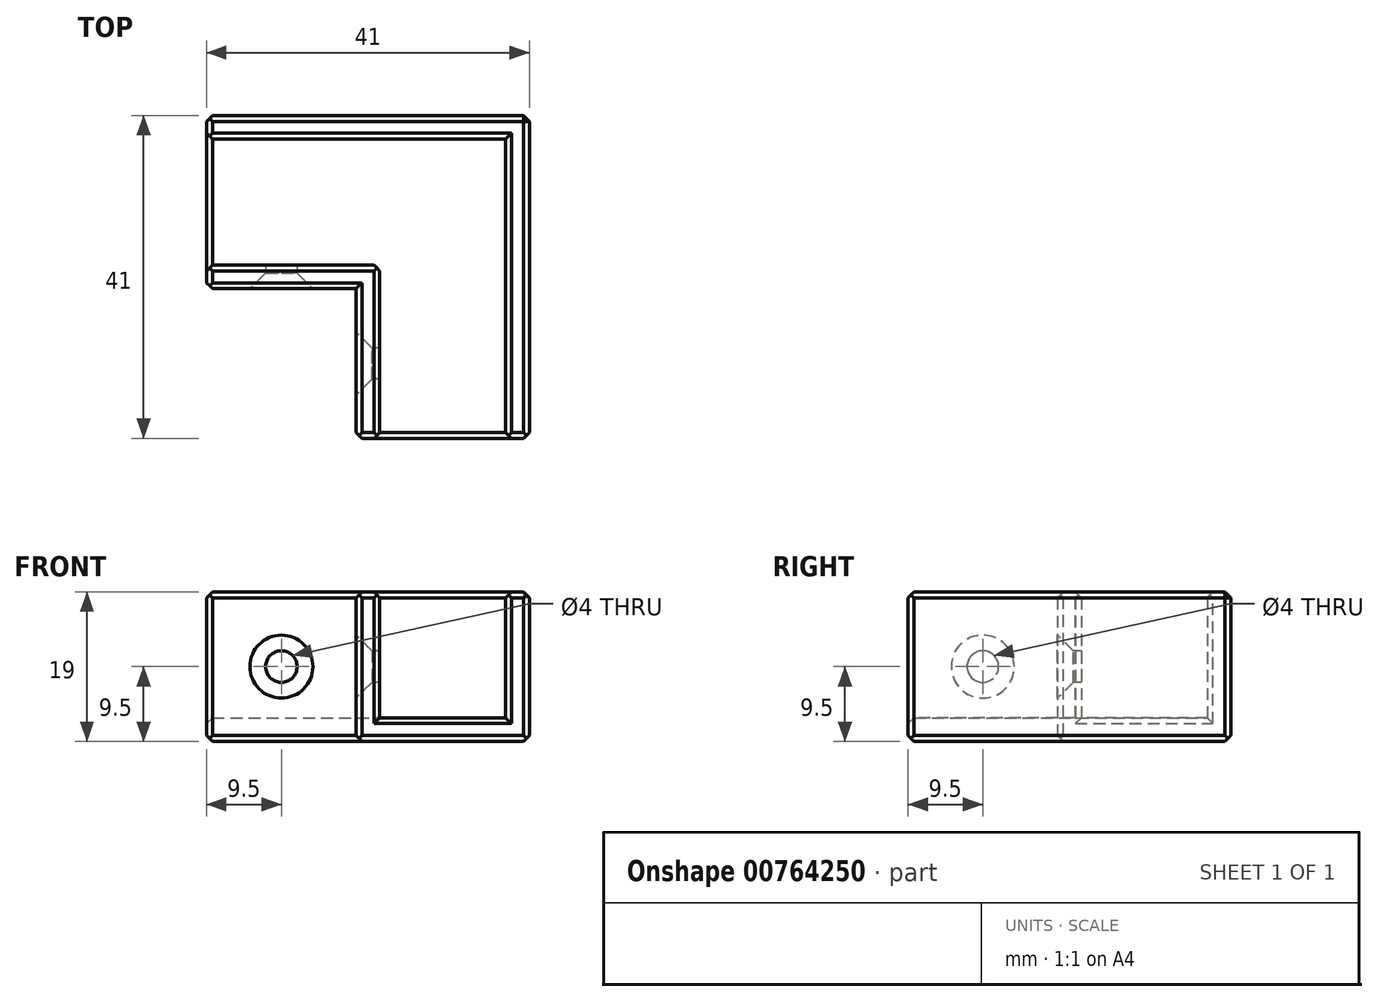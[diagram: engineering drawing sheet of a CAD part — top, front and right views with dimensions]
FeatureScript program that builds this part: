
annotation { "Feature Type Name" : "Feature", "Feature Type Description" : "" }
export const myFeature = defineFeature(function(context is Context, id is Id, definition is map)
    precondition{}
    {
        {
            var Q0;
            Q0=qCreatedBy(makeId("Top.planeOp"),FACE);
            var sketch = newSketch(context, id + "F0", { "sketchPlane" : qUnion([Q0])});
            skLineSegment(sketch, "E0.bottom", {"start": v(0, 0) * mm, "end": v(41, 0) * mm});
            skLineSegment(sketch, "E0.top", {"start": v(0, 22) * mm, "end": v(41, 22) * mm});
            skLineSegment(sketch, "E0.left", {"start": v(0, 0) * mm, "end": v(0, 22) * mm});
            skLineSegment(sketch, "E0.right", {"start": v(41, 0) * mm, "end": v(41, 22) * mm});
            skLineSegment(sketch, "E1", {"start": v(0, 0) * mm, "end": v(19, 0) * mm});
            skLineSegment(sketch, "E2.bottom", {"start": v(19, 0) * mm, "end": v(41, 0) * mm});
            skLineSegment(sketch, "E2.top", {"start": v(19, -19) * mm, "end": v(41, -19) * mm});
            skLineSegment(sketch, "E2.left", {"start": v(19, 0) * mm, "end": v(19, -19) * mm});
            skLineSegment(sketch, "E2.right", {"start": v(41, 0) * mm, "end": v(41, -19) * mm});
            skSolve(sketch);
        }
        {
            var Q0;
            Q0=makeQuery(id+"F0.imprint","IMPRINT",FACE,{"disambiguationData":[TD([[makeQuery(id+"F0.imprint","IMPRINT",EDGE,{"derivedFrom":sQuery(id+"F0.wireOp",EDGE,"E0.top")}),-1.0]])]});
            var Q1;
            Q1=makeQuery(id+"F0.imprint","IMPRINT",FACE,{"disambiguationData":[TD([[makeQuery(id+"F0.imprint","IMPRINT",EDGE,{"derivedFrom":sQuery(id+"F0.wireOp",EDGE,"E2.top")}),1.0]])]});
            extrude(context, id + "F1", {"entities" : qUnion([Q0, Q1]), "depth" : 3 * mm, "offsetDistance" : 25 * mm});
        }
        {
            var Q0;
            Q0=makeQuery(id+"F1.opExtrude","CAP_FACE",FACE,{"disambiguationData":[OSD([sQuery(id+"F0.wireOp",EDGE,"E0.bottom"),sQuery(id+"F0.wireOp",EDGE,"E0.top"),sQuery(id+"F0.wireOp",EDGE,"E0.left"),sQuery(id+"F0.wireOp",EDGE,"E0.right"),sQuery(id+"F0.wireOp",EDGE,"E2.top"),sQuery(id+"F0.wireOp",EDGE,"E2.left"),sQuery(id+"F0.wireOp",EDGE,"E2.right")])],"isStart":false});
            var sketch = newSketch(context, id + "F2", { "sketchPlane" : qUnion([Q0])});
            skLineSegment(sketch, "E3.bottom", {"start": v(0, 22) * mm, "end": v(41, 22) * mm});
            skLineSegment(sketch, "E3.top", {"start": v(0, 19) * mm, "end": v(41, 19) * mm});
            skLineSegment(sketch, "E3.left", {"start": v(0, 22) * mm, "end": v(0, 19) * mm});
            skLineSegment(sketch, "E3.right", {"start": v(41, 22) * mm, "end": v(41, 19) * mm});
            skLineSegment(sketch, "E4.bottom", {"start": v(19, 0) * mm, "end": v(0, 0) * mm});
            skLineSegment(sketch, "E4.top", {"start": v(19, 3) * mm, "end": v(0, 3) * mm});
            skLineSegment(sketch, "E4.left", {"start": v(19, 0) * mm, "end": v(19, 3) * mm});
            skLineSegment(sketch, "E4.right", {"start": v(0, 0) * mm, "end": v(0, 3) * mm});
            skLineSegment(sketch, "E5.bottom", {"start": v(19, 3) * mm, "end": v(22, 3) * mm});
            skLineSegment(sketch, "E5.top", {"start": v(19, -19) * mm, "end": v(22, -19) * mm});
            skLineSegment(sketch, "E5.left", {"start": v(19, 3) * mm, "end": v(19, -19) * mm});
            skLineSegment(sketch, "E5.right", {"start": v(22, 3) * mm, "end": v(22, -19) * mm});
            skLineSegment(sketch, "E6.bottom", {"start": v(41, -19) * mm, "end": v(38, -19) * mm});
            skLineSegment(sketch, "E6.top", {"start": v(41, 19) * mm, "end": v(38, 19) * mm});
            skLineSegment(sketch, "E6.left", {"start": v(41, -19) * mm, "end": v(41, 19) * mm});
            skLineSegment(sketch, "E6.right", {"start": v(38, -19) * mm, "end": v(38, 19) * mm});
            skSolve(sketch);
        }
        {
            var Q0;
            Q0=makeQuery(id+"F2.imprint","IMPRINT",FACE,{"disambiguationData":[TD([[makeQuery(id+"F2.imprint","IMPRINT",EDGE,{"derivedFrom":sQuery(id+"F2.wireOp",EDGE,"E3.bottom")}),-1.0]])]});
            var Q1;
            Q1=makeQuery(id+"F2.imprint","IMPRINT",FACE,{"disambiguationData":[TD([[makeQuery(id+"F2.imprint","IMPRINT",EDGE,{"derivedFrom":sQuery(id+"F2.wireOp",EDGE,"E6.bottom")}),1.0]])]});
            var Q2;
            {var subQ2=sQuery(id+"F2.wireOp",EDGE,"E5.bottom");Q2=makeQuery(id+"F2.imprint","IMPRINT",FACE,{"disambiguationData":[TD([[makeQuery(id+"F2.imprint","IMPRINT",EDGE,{"derivedFrom":subQ2}),-1.0]])]});}
            var Q3;
            {var subQ0=sQuery(id+"F2.wireOp",EDGE,"E4.bottom");Q3=makeQuery(id+"F2.imprint","IMPRINT",FACE,{"disambiguationData":[TD([[makeQuery(id+"F2.imprint","IMPRINT",EDGE,{"derivedFrom":subQ0}),1.0]])]});}
            extrude(context, id + "F3", {"entities" : qUnion([Q0, Q1, Q2, Q3]), "operationType" : NewBodyOperationType.ADD, "depth" : 16 * mm, "offsetDistance" : 25 * mm});
        }
        {
            var Q0;
            Q0=makeQuery(id+"F3.boolean.opBoolean","MERGE",FACE,{"derivedFrom":[makeQuery(id+"F1.opExtrude","SWEPT_FACE",FACE,{"disambiguationData":[OSD([sQuery(id+"F0.wireOp",EDGE,"E0.bottom")])]}),makeQuery(id+"F3.opExtrude","SWEPT_FACE",FACE,{"disambiguationData":[OSD([sQuery(id+"F2.wireOp",EDGE,"E4.bottom")])]})]});
            var sketch = newSketch(context, id + "F4", { "sketchPlane" : qUnion([Q0])});
            skLineSegment(sketch, "E7", {"start": v(0, 19) * mm, "end": v(19, 0) * mm});
            skLineSegment(sketch, "E8", {"start": v(19, 0) * mm, "end": v(19, 19) * mm});
            skLineSegment(sketch, "E9", {"start": v(19, 19) * mm, "end": v(0, 0) * mm});
            skPoint(sketch, "E10", {"position": v(9.5, 9.5) * mm});
            skSolve(sketch);
        }
        {
            var Q0;
            Q0=sQuery(id+"F4.wireOp",VERTEX,"E10");
            var Q1;
            Q1=makeQuery(id+"F1.opExtrude","SWEPT_BODY",BODY,{"disambiguationData":[OSD([sQuery(id+"F0.wireOp",EDGE,"E0.bottom"),sQuery(id+"F0.wireOp",EDGE,"E0.top"),sQuery(id+"F0.wireOp",EDGE,"E0.left"),sQuery(id+"F0.wireOp",EDGE,"E0.right"),sQuery(id+"F0.wireOp",EDGE,"E2.top"),sQuery(id+"F0.wireOp",EDGE,"E2.left"),sQuery(id+"F0.wireOp",EDGE,"E2.right")])]});
            hole(context, id + "F5", {"style" : HoleStyle.C_SINK, "endStyle" : HoleEndStyle.BLIND, "holeDiameter" : 4 * mm, "cSinkDiameter" : 8 * mm, "cSinkAngle" : 90 * degree, "majorDiameter" : 5 * mm, "holeDepth" : 12 * mm, "isTappedThrough" : true, "tappedDepth" : 12 * mm, "tapClearance" : 3, "locations" : qUnion([Q0]), "scope" : qUnion([Q1])});
        }
        {
            var Q0;
            Q0=makeQuery(id+"F3.boolean.opBoolean","MERGE",FACE,{"derivedFrom":[makeQuery(id+"F1.opExtrude","SWEPT_FACE",FACE,{"disambiguationData":[OSD([sQuery(id+"F0.wireOp",EDGE,"E2.left")])]}),makeQuery(id+"F3.opExtrude","SWEPT_FACE",FACE,{"disambiguationData":[OSD([sQuery(id+"F2.wireOp",EDGE,"E5.left")])]})]});
            var sketch = newSketch(context, id + "F6", { "sketchPlane" : qUnion([Q0])});
            skLineSegment(sketch, "E11", {"start": v(0, 19) * mm, "end": v(19, 0) * mm});
            skLineSegment(sketch, "E12", {"start": v(19, 0) * mm, "end": v(19, 19) * mm});
            skLineSegment(sketch, "E13", {"start": v(19, 19) * mm, "end": v(0, 0) * mm});
            skPoint(sketch, "E14", {"position": v(9.5, 9.5) * mm});
            skSolve(sketch);
        }
        {
            var Q0;
            Q0=sQuery(id+"F6.wireOp",VERTEX,"E14");
            var Q1;
            Q1=makeQuery(id+"F1.opExtrude","SWEPT_BODY",BODY,{"disambiguationData":[OSD([sQuery(id+"F0.wireOp",EDGE,"E0.bottom"),sQuery(id+"F0.wireOp",EDGE,"E0.top"),sQuery(id+"F0.wireOp",EDGE,"E0.left"),sQuery(id+"F0.wireOp",EDGE,"E0.right"),sQuery(id+"F0.wireOp",EDGE,"E2.top"),sQuery(id+"F0.wireOp",EDGE,"E2.left"),sQuery(id+"F0.wireOp",EDGE,"E2.right")])]});
            hole(context, id + "F7", {"style" : HoleStyle.C_SINK, "endStyle" : HoleEndStyle.BLIND, "holeDiameter" : 4 * mm, "cSinkDiameter" : 8 * mm, "cSinkAngle" : 90 * degree, "majorDiameter" : 5 * mm, "holeDepth" : 12 * mm, "isTappedThrough" : true, "tappedDepth" : 12 * mm, "tapClearance" : 3, "locations" : qUnion([Q0]), "scope" : qUnion([Q1])});
        }
        {
            var Q0;
            Q0=makeQuery(id+"F3.boolean.opBoolean","MERGE",FACE,{"derivedFrom":[makeQuery(id+"F1.opExtrude","SWEPT_FACE",FACE,{"disambiguationData":[OSD([sQuery(id+"F0.wireOp",EDGE,"E2.top")])]}),makeQuery(id+"F3.opExtrude","SWEPT_FACE",FACE,{"disambiguationData":[OSD([sQuery(id+"F2.wireOp",EDGE,"E5.top")])]}),makeQuery(id+"F3.opExtrude","SWEPT_FACE",FACE,{"disambiguationData":[OSD([sQuery(id+"F2.wireOp",EDGE,"E6.bottom")])]})]});
            chamfer(context, id + "F8", {"entities" : qUnion([Q0]), "width" : 0.75 * mm, "tangentPropagation" : true});
        }
        {
            var Q0;
            Q0=makeQuery(id+"F3.boolean.opBoolean","MERGE",FACE,{"derivedFrom":[makeQuery(id+"F1.opExtrude","SWEPT_FACE",FACE,{"disambiguationData":[OSD([sQuery(id+"F0.wireOp",EDGE,"E0.left")])]}),makeQuery(id+"F3.opExtrude","SWEPT_FACE",FACE,{"disambiguationData":[OSD([sQuery(id+"F2.wireOp",EDGE,"E3.left")])]}),makeQuery(id+"F3.opExtrude","SWEPT_FACE",FACE,{"disambiguationData":[OSD([sQuery(id+"F2.wireOp",EDGE,"E4.right")])]})]});
            chamfer(context, id + "F9", {"entities" : qUnion([Q0]), "width" : 0.75 * mm, "tangentPropagation" : true});
        }
        {
            var Q0;
            Q0=makeQuery(id+"F3.opExtrude","CAP_EDGE",EDGE,{"disambiguationData":[OSD([sQuery(id+"F2.wireOp",EDGE,"E5.left")])],"isStart":false});
            var Q1;
            Q1=makeQuery(id+"F3.opExtrude","CAP_EDGE",EDGE,{"disambiguationData":[OSD([sQuery(id+"F2.wireOp",EDGE,"E4.bottom")])],"isStart":false});
            var Q2;
            Q2=makeQuery(id+"F3.opExtrude","CAP_EDGE",EDGE,{"disambiguationData":[OSD([sQuery(id+"F2.wireOp",EDGE,"E4.top"),sQuery(id+"F2.wireOp",EDGE,"E5.bottom")])],"isStart":false});
            var Q3;
            Q3=makeQuery(id+"F3.opExtrude","CAP_EDGE",EDGE,{"disambiguationData":[OSD([sQuery(id+"F2.wireOp",EDGE,"E5.right")])],"isStart":false});
            var Q4;
            Q4=makeQuery(id+"F3.opExtrude","CAP_EDGE",EDGE,{"disambiguationData":[OSD([sQuery(id+"F2.wireOp",EDGE,"E6.right")])],"isStart":false});
            var Q5;
            Q5=makeQuery(id+"F3.opExtrude","CAP_EDGE",EDGE,{"disambiguationData":[OSD([sQuery(id+"F2.wireOp",EDGE,"E3.top")])],"isStart":false});
            var Q6;
            Q6=makeQuery(id+"F3.opExtrude","CAP_EDGE",EDGE,{"disambiguationData":[OSD([sQuery(id+"F2.wireOp",EDGE,"E3.bottom")])],"isStart":false});
            var Q7;
            Q7=makeQuery(id+"F3.opExtrude","CAP_EDGE",EDGE,{"disambiguationData":[OSD([sQuery(id+"F2.wireOp",EDGE,"E3.right"),sQuery(id+"F2.wireOp",EDGE,"E6.left")])],"isStart":false});
            var Q8;
            Q8=makeQuery(id+"F3.boolean.opBoolean","MERGE",EDGE,{"derivedFrom":[makeQuery(id+"F1.opExtrude","SWEPT_EDGE",EDGE,{"disambiguationData":[OSD([sQuery(id+"F0.wireOp",EDGE,"E0.top"),sQuery(id+"F0.wireOp",EDGE,"E0.right")])]}),makeQuery(id+"F3.opExtrude","SWEPT_EDGE",EDGE,{"disambiguationData":[OSD([sQuery(id+"F2.wireOp",EDGE,"E3.bottom"),sQuery(id+"F2.wireOp",EDGE,"E3.right")])]})]});
            chamfer(context, id + "F10", {"entities" : qUnion([Q0, Q1, Q2, Q3, Q4, Q5, Q6, Q7, Q8]), "width" : 0.75 * mm, "tangentPropagation" : true});
        }
        {
            var Q0;
            Q0=makeQuery(id+"F3.opExtrude","SWEPT_EDGE",EDGE,{"disambiguationData":[OSD([sQuery(id+"F2.wireOp",EDGE,"E5.bottom"),sQuery(id+"F2.wireOp",EDGE,"E5.right")])]});
            chamfer(context, id + "F11", {"entities" : qUnion([Q0]), "width" : 0.75 * mm, "tangentPropagation" : true});
        }
        {
            var Q0;
            Q0=makeQuery(id+"F1.opExtrude","CAP_EDGE",EDGE,{"disambiguationData":[OSD([sQuery(id+"F0.wireOp",EDGE,"E2.left")])],"isStart":true});
            var Q1;
            Q1=makeQuery(id+"F1.opExtrude","CAP_EDGE",EDGE,{"disambiguationData":[OSD([sQuery(id+"F0.wireOp",EDGE,"E0.bottom")])],"isStart":true});
            var Q2;
            Q2=makeQuery(id+"F1.opExtrude","CAP_EDGE",EDGE,{"disambiguationData":[OSD([sQuery(id+"F0.wireOp",EDGE,"E0.right"),sQuery(id+"F0.wireOp",EDGE,"E2.right")])],"isStart":true});
            var Q3;
            Q3=makeQuery(id+"F1.opExtrude","CAP_EDGE",EDGE,{"disambiguationData":[OSD([sQuery(id+"F0.wireOp",EDGE,"E0.top")])],"isStart":true});
            chamfer(context, id + "F12", {"entities" : qUnion([Q0, Q1, Q2, Q3]), "width" : 0.75 * mm, "tangentPropagation" : true});
        }
    });
